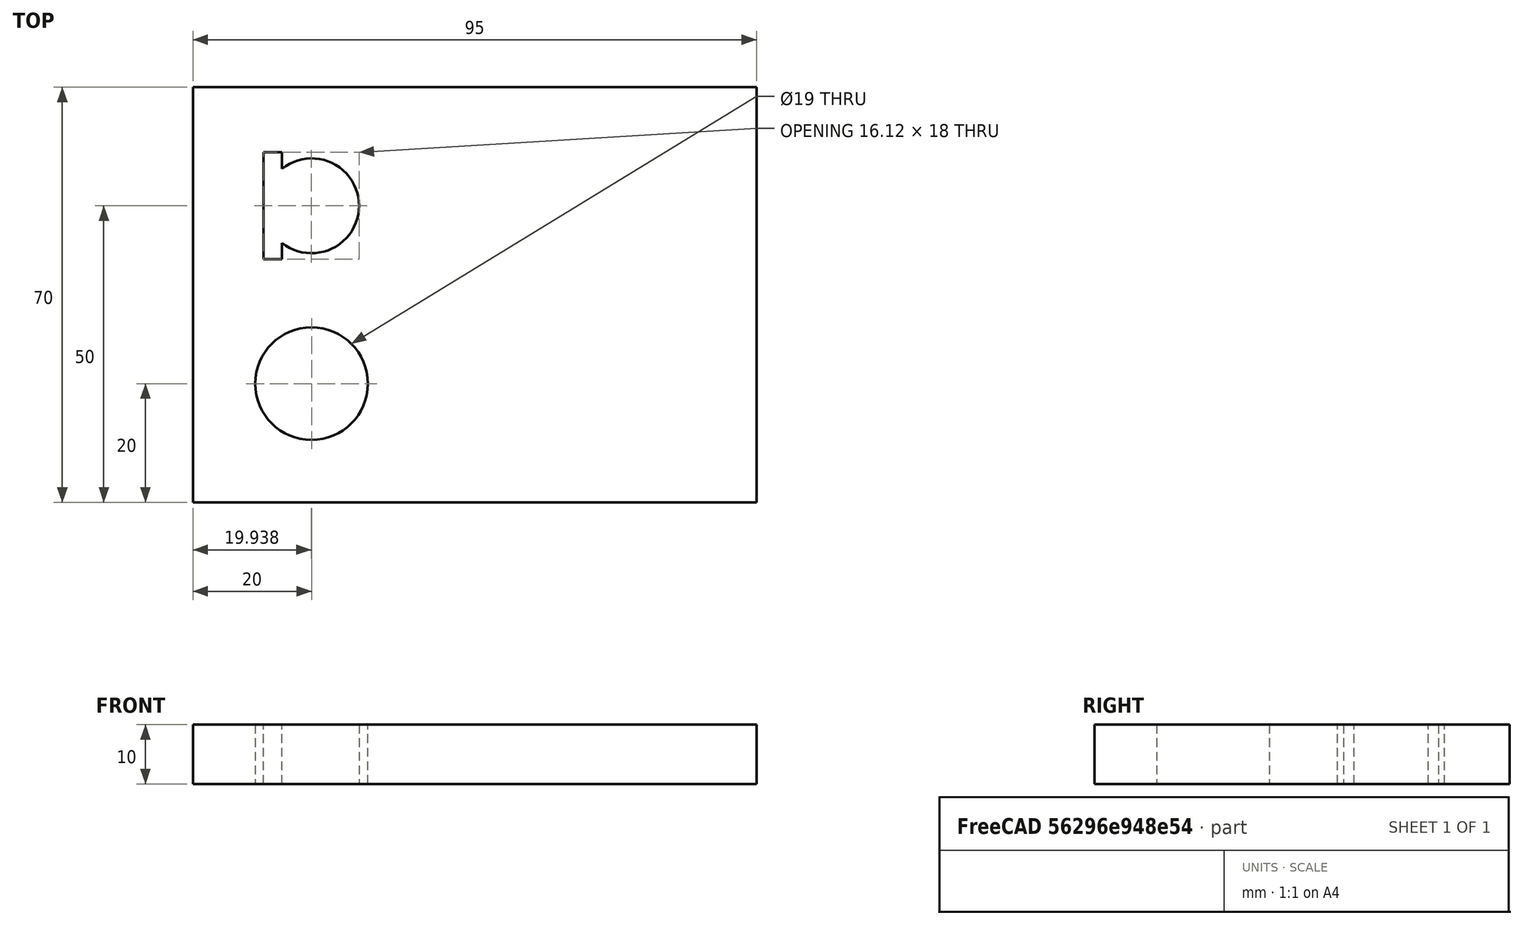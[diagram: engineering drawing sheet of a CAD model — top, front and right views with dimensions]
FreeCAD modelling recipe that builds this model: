
FCSTD DOCUMENT  (FreeCAD 0.19R24276 (Git))
Label: BLDC_holder_part2_middle_v1
License: All rights reserved
LicenseURL: http://en.wikipedia.org/wiki/All_rights_reserved
objects: Sketcher::SketchObject×1, PartDesign::Pad×1, PartDesign::Body×1
note: 4 computed .brp shape members not serialized (recipe doc carries the construction recipe); baked Part::Feature solids carry a one-line shape summary decoded from their .brp

FEATURE [Sketcher::SketchObject] Sketch  label="Sketch_D16_D19_L70X75"
  FullyConstrained = true
  MapMode = 5
  Support = -> [XY_Plane]
  sketch-geometry (13):
    g0: ArcOfCircle CenterX=0 CenterY=0 CenterZ=0 NormalX=0 NormalY=0 NormalZ=1 AngleXU=0 Radius=8 StartAngle=4.03726 EndAngle=8.52911
    g1: Circle CenterX=0 CenterY=-30 CenterZ=0 NormalX=0 NormalY=0 NormalZ=1 AngleXU=0 Radius=9.5
    g2: LineSegment StartX=-20 StartY=20 StartZ=0 EndX=75 EndY=20 EndZ=0
    g3: LineSegment StartX=75 StartY=20 StartZ=0 EndX=75 EndY=-50 EndZ=0
    g4: LineSegment StartX=75 StartY=-50 StartZ=0 EndX=-20 EndY=-50 EndZ=0
    g5: LineSegment StartX=-20 StartY=-50 StartZ=0 EndX=-20 EndY=20 EndZ=0
    g6: LineSegment StartX=0 StartY=0 StartZ=0 EndX=8 EndY=0 EndZ=0
    g7: LineSegment StartX=-5 StartY=-9 StartZ=0 EndX=-8.125 EndY=-9 EndZ=0
    g8: LineSegment StartX=-8.125 StartY=-9 StartZ=0 EndX=-8.125 EndY=9 EndZ=0
    g9: LineSegment StartX=-8.125 StartY=9 StartZ=0 EndX=-5 EndY=9 EndZ=0
    g10: LineSegment StartX=-5 StartY=9 StartZ=0 EndX=-5 EndY=6.245 EndZ=0
    g11: LineSegment StartX=0 StartY=0 StartZ=0 EndX=-8.125 EndY=0 EndZ=0
    g12: LineSegment StartX=-5 StartY=-6.245 StartZ=0 EndX=-5 EndY=-9 EndZ=0
  constraints (38):
    c: Coincident(g0,g-1)
    c: Diameter(g0) = 16
    c: PointOnObject(g1,g-2)
    c: Diameter(g1) = 19
    c: DistanceY(g1,g0) = 30
    c: Coincident(g2,g3)
    c: Coincident(g3,g4)
    c: Coincident(g4,g5)
    c: Coincident(g5,g2)
    c: Horizontal(g2)
    c: Horizontal(g4)
    c: Vertical(g3)
    c: Vertical(g5)
    c: DistanceX(g0,g2) = 75
    c: DistanceY(g4,g1) = 20
    c: DistanceX(g2,g0) = 20
    c: DistanceY(g3,g2) = 70
    c: Coincident(g6,g0)
    c: PointOnObject(g6,g0)
    c: Horizontal(g6)
    c: DistanceX(g7,g6) = 13
    c: Coincident(g7,g8)
    c: Coincident(g8,g9)
    c: Coincident(g9,g10)
    c: Coincident(g12,g7)
    c: Horizontal(g7)
    c: Horizontal(g9)
    c: Vertical(g8)
    c: Vertical(g10)
    c: DistanceX(g7,g7) = 3.125
    c: Coincident(g11,g0)
    c: PointOnObject(g11,g-1)
    c: Symmetric(g7,g8,g11)
    c: DistanceY(g8,g8) = 18
    c: PointOnObject(g0,g10)
    c: Coincident(g10,g0)
    c: Tangent(g10,g12)
    c: PointOnObject(g12,g0)
FEATURE [PartDesign::Pad] Pad  label="Pad_h10"
  Direction = (1,1,1)
  Length = 10
  Length2 = 100
  Profile = -> Sketch
  Type = 0
FEATURE [PartDesign::Body] Body
  Group = -> [Sketch,Pad]
  Origin = -> Origin
  Tip = -> Pad
